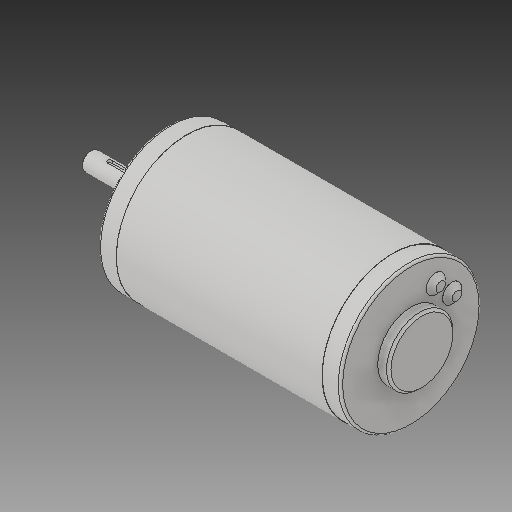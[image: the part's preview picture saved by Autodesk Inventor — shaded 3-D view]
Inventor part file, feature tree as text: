
AUTODESK INVENTOR PART (.ipt)
format: ipt  version: 2017 (Build 210142000, 142)  size: 164,352 bytes
history: native  units: in
note: dims shown in document units (in); Inventor stores cm internally (conversion verified against a paired STEP export)
features: chamfer x1
ambient origin geometry x8: Origin, YZ Plane, XZ Plane, XY Plane, X Axis, Y Axis, Z Axis, Center Point
bodies: Solid1 (feature_tree)
feature tree (1):
  chamfer  "Chamfer3"  [1 undecoded]
note: 1 required parameter value undecoded (feature->parameter linkage not recoverable at this tier; creation-order binding heuristic only, values carry confidence <= 0.55)
